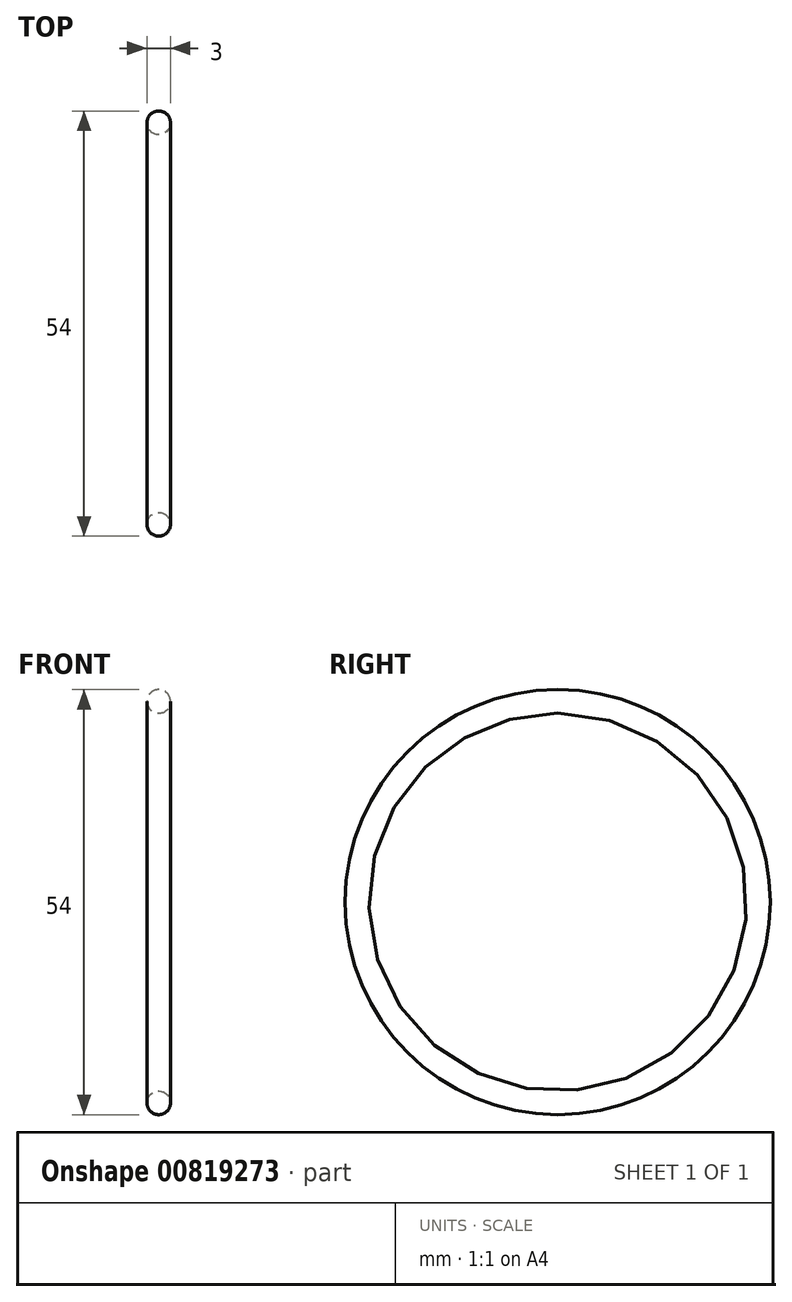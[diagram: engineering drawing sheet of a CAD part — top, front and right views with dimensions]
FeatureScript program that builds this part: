
annotation { "Feature Type Name" : "Feature", "Feature Type Description" : "" }
export const myFeature = defineFeature(function(context is Context, id is Id, definition is map)
    precondition{}
    {
        {
            var Q0;
            Q0=qCreatedBy(makeId("Front.planeOp"),FACE);
            var sketch = newSketch(context, id + "F0", { "sketchPlane" : qUnion([Q0])});
            skLineSegment(sketch, "E0", {"start": v(-11.63, 0) * mm, "end": v(11.63, 0) * mm, "construction": true});
            skCircle(sketch, "E1", {"center": v(0, 25.5) * mm, "radius": 1.5 * mm});
            skSolve(sketch);
        }
        {
            var Q0;
            Q0=makeQuery(id+"F0.imprint","IMPRINT",FACE,{"disambiguationData":[TD([[makeQuery(id+"F0.imprint","IMPRINT",EDGE,{"derivedFrom":sQuery(id+"F0.wireOp",EDGE,"E1")}),1.0]])]});
            var Q1;
            Q1=sQuery(id+"F0.wireOp",EDGE,"E0");
            revolve(context, id + "F1", {"surfaceOperationType" : NewSurfaceOperationType.NEW, "entities" : qUnion([Q0]), "axis" : qUnion([Q1]), "revolveType" : RevolveType.FULL});
        }
    });
